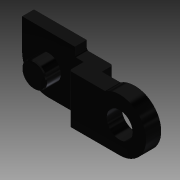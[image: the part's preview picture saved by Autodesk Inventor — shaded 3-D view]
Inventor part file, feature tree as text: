
AUTODESK INVENTOR PART (.ipt)
format: ipt  version: 2013 (Build 170138000, 138)  size: 106,496 bytes
history: native  units: in
note: dims shown in document units (in); Inventor stores cm internally (conversion verified against a paired STEP export)
features: other x1, imported_body x1, extrude x1, sketch x1
ambient origin geometry x8: Origin, YZ Plane, XZ Plane, XY Plane, X Axis, Y Axis, Z Axis, Center Point
feature tree (4):
  other  "TETRIX_TT_LINK_2_2011"
  imported_body  "Base1"
  extrude  "Extrusion1"  [1 undecoded]
  sketch  "Sketch2"  dims[d0=0.009in d1=0.0in]
note: 1 required parameter value undecoded (feature->parameter linkage not recoverable at this tier; creation-order binding heuristic only, values carry confidence <= 0.55)
